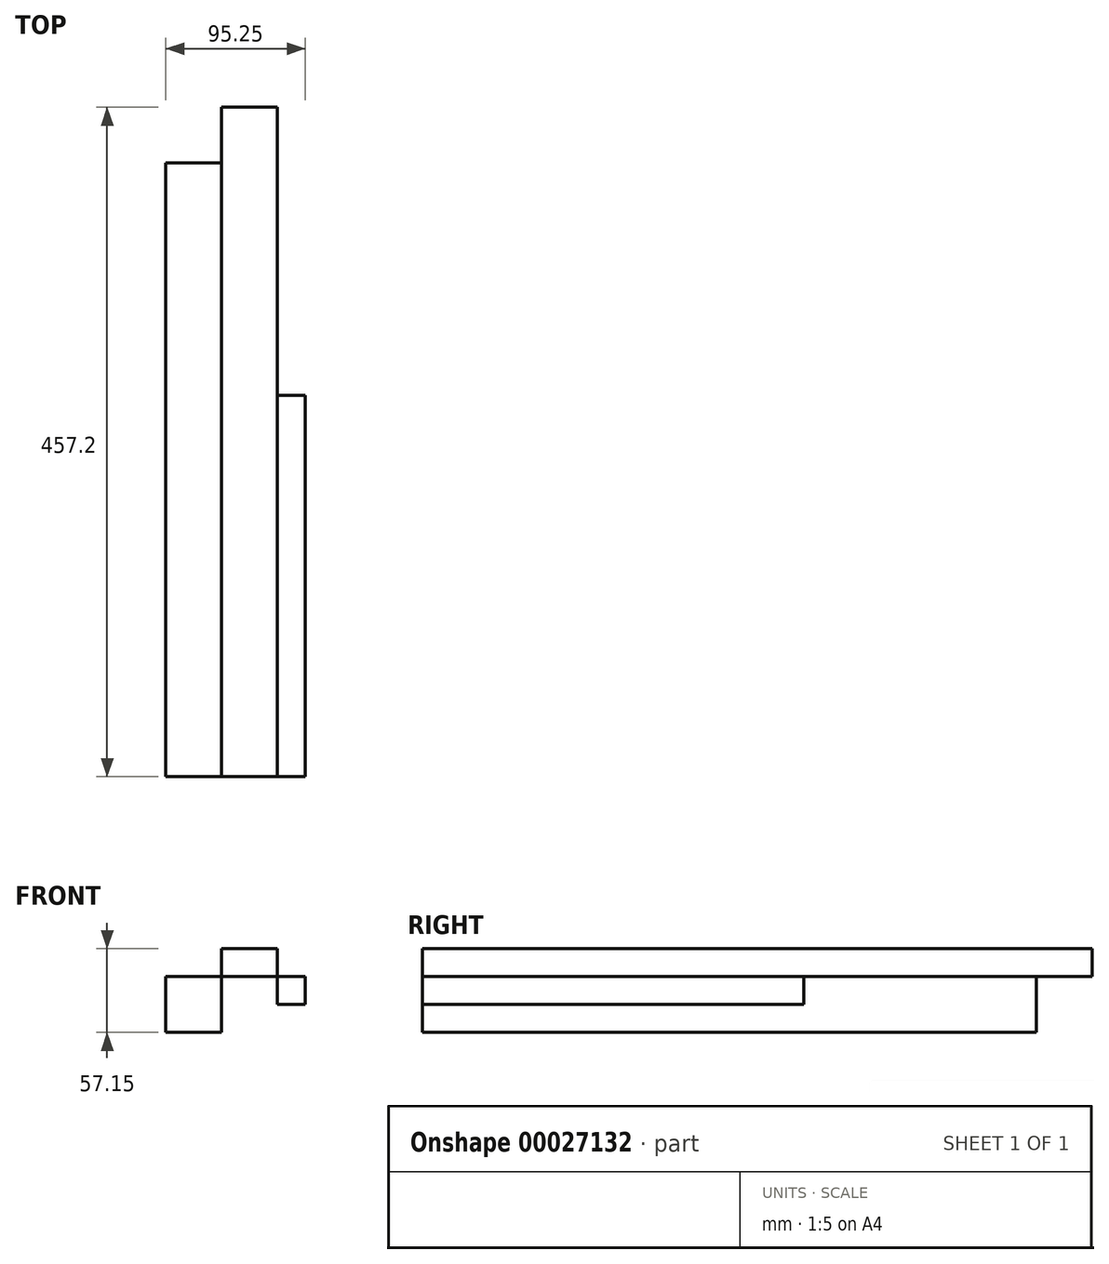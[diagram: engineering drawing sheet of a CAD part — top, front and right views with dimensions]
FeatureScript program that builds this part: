
annotation { "Feature Type Name" : "Feature", "Feature Type Description" : "" }
export const myFeature = defineFeature(function(context is Context, id is Id, definition is map)
    precondition{}
    {
        {
            var Q0;
            Q0=qCreatedBy(makeId("Front.planeOp"),FACE);
            var sketch = newSketch(context, id + "F0", { "sketchPlane" : qUnion([Q0])});
            skLineSegment(sketch, "E0.bottom", {"start": v(0, 0) * mm, "end": v(38.1, 0) * mm});
            skLineSegment(sketch, "E0.top", {"start": v(0, 19.05) * mm, "end": v(38.1, 19.05) * mm});
            skLineSegment(sketch, "E0.left", {"start": v(0, 0) * mm, "end": v(0, 19.05) * mm});
            skLineSegment(sketch, "E0.right", {"start": v(38.1, 0) * mm, "end": v(38.1, 19.05) * mm});
            skLineSegment(sketch, "E1.bottom", {"start": v(0, 0) * mm, "end": v(-38.1, 0) * mm});
            skLineSegment(sketch, "E1.top", {"start": v(0, -38.1) * mm, "end": v(-38.1, -38.1) * mm});
            skLineSegment(sketch, "E1.left", {"start": v(0, 0) * mm, "end": v(0, -38.1) * mm});
            skLineSegment(sketch, "E1.right", {"start": v(-38.1, 0) * mm, "end": v(-38.1, -38.1) * mm});
            skLineSegment(sketch, "E2.bottom", {"start": v(38.1, 0) * mm, "end": v(57.15, 0) * mm});
            skLineSegment(sketch, "E2.top", {"start": v(38.1, -19.05) * mm, "end": v(57.15, -19.05) * mm});
            skLineSegment(sketch, "E2.left", {"start": v(38.1, 0) * mm, "end": v(38.1, -19.05) * mm});
            skLineSegment(sketch, "E2.right", {"start": v(57.15, 0) * mm, "end": v(57.15, -19.05) * mm});
            skSolve(sketch);
        }
        {
            var Q0;
            Q0=makeQuery(id+"F0.imprint","IMPRINT",FACE,{"disambiguationData":[TD([[makeQuery(id+"F0.imprint","IMPRINT",EDGE,{"derivedFrom":sQuery(id+"F0.wireOp",EDGE,"E0.top")}),-1.0]])]});
            extrude(context, id + "F1", {"entities" : qUnion([Q0]), "oppositeDirection" : true, "depth" : 457.2 * mm});
        }
        {
            var Q0;
            Q0=makeQuery(id+"F0.imprint","IMPRINT",FACE,{"disambiguationData":[TD([[makeQuery(id+"F0.imprint","IMPRINT",EDGE,{"derivedFrom":sQuery(id+"F0.wireOp",EDGE,"E1.bottom")}),1.0]])]});
            extrude(context, id + "F2", {"entities" : qUnion([Q0]), "oppositeDirection" : true, "depth" : 419.1 * mm});
        }
        {
            var Q0;
            Q0=makeQuery(id+"F0.imprint","IMPRINT",FACE,{"disambiguationData":[TD([[makeQuery(id+"F0.imprint","IMPRINT",EDGE,{"derivedFrom":sQuery(id+"F0.wireOp",EDGE,"E2.bottom")}),-1.0]])]});
            extrude(context, id + "F3", {"entities" : qUnion([Q0]), "oppositeDirection" : true, "depth" : 260.35 * mm});
        }
    });
